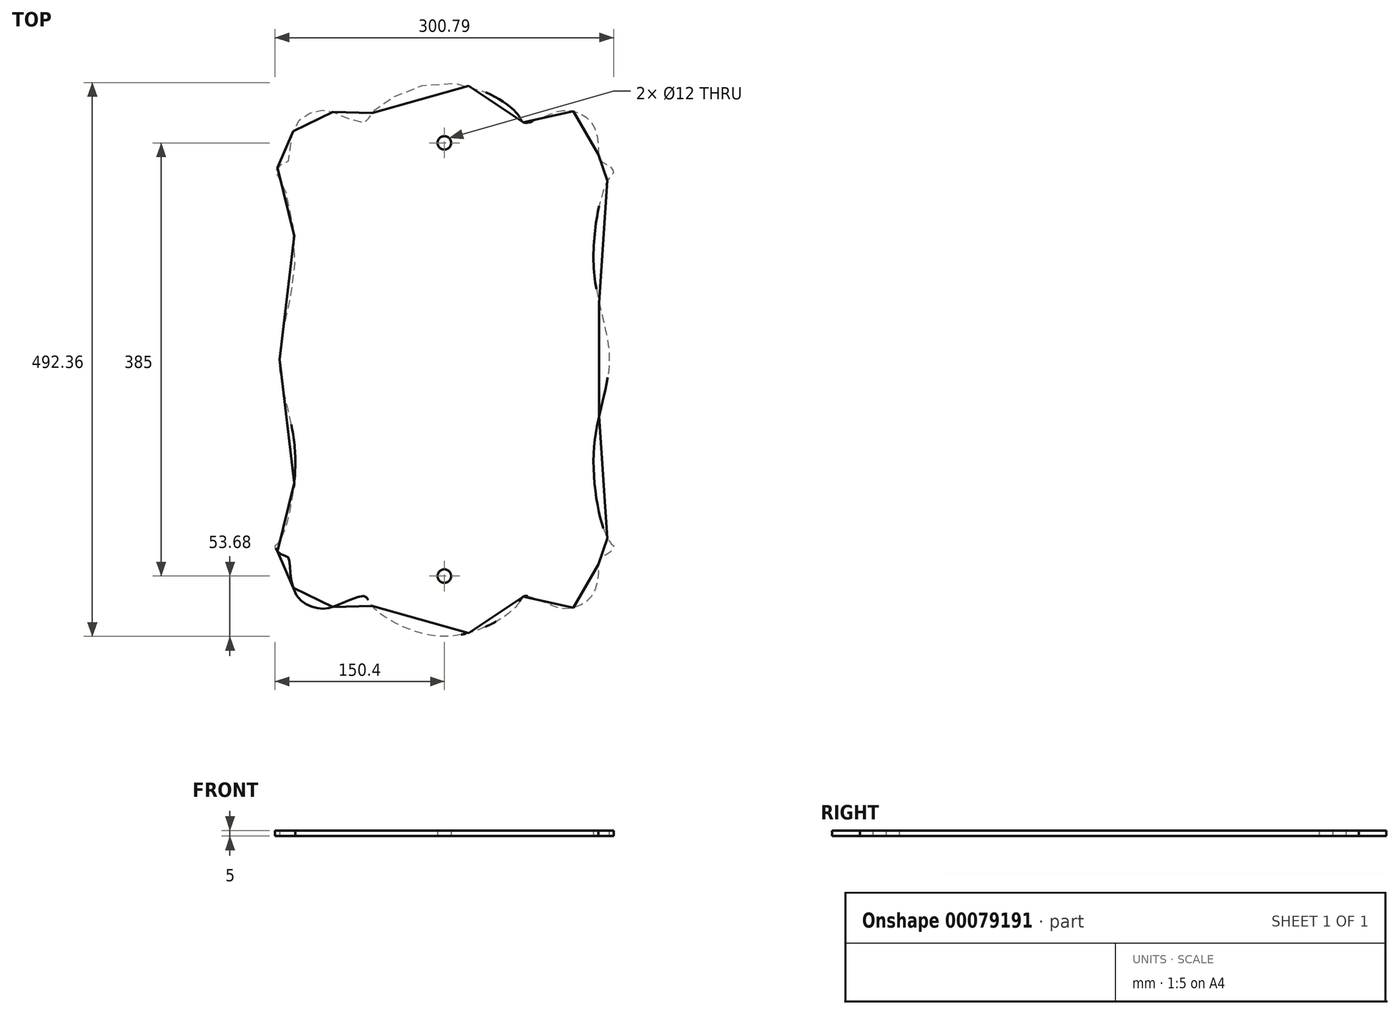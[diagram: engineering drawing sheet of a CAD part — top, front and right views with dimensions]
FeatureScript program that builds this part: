
annotation { "Feature Type Name" : "Feature", "Feature Type Description" : "" }
export const myFeature = defineFeature(function(context is Context, id is Id, definition is map)
    precondition{}
    {
        {
            var Q0;
            Q0=qCreatedBy(makeId("Top.planeOp"),FACE);
            var sketch = newSketch(context, id + "F0", { "sketchPlane" : qUnion([Q0])});
            skPoint(sketch, "E0", {"position": v(150.32, -165.76) * mm});
            skPoint(sketch, "E1", {"position": v(107.37, -221.56) * mm});
            skPoint(sketch, "E2", {"position": v(69.02, -211.72) * mm});
            skPoint(sketch, "E3", {"position": v(0, -246.18) * mm});
            skPoint(sketch, "E4", {"position": v(138.05, -177.25) * mm});
            skPoint(sketch, "E5", {"position": v(146.48, 0) * mm});
            skPoint(sketch, "E6", {"position": v(132.68, -82.88) * mm});
            skLineSegment(sketch, "E7", {"start": v(0, 292) * mm, "end": v(0, -246.18) * mm, "construction": true});
            skPoint(sketch, "E8.MirrorP", {"position": v(-146.48, 0) * mm});
            skPoint(sketch, "E9.MirrorP", {"position": v(-132.68, -82.88) * mm});
            skPoint(sketch, "E10.MirrorP", {"position": v(-150.32, -165.76) * mm});
            skPoint(sketch, "E11.MirrorP", {"position": v(-138.05, -177.25) * mm});
            skPoint(sketch, "E12.MirrorP", {"position": v(-107.37, -221.56) * mm});
            skPoint(sketch, "E13.MirrorP", {"position": v(-69.02, -211.72) * mm});
            skPoint(sketch, "E14", {"position": v(0, 0) * mm});
            skPoint(sketch, "E15", {"position": v(-146.25, -161.4) * mm});
            skPoint(sketch, "E16", {"position": v(-136.87, -189.28) * mm});
            skPoint(sketch, "E17", {"position": v(-146.26, -172.33) * mm});
            skPoint(sketch, "E18", {"position": v(-131.04, -210.06) * mm});
            skPoint(sketch, "E19", {"position": v(-94.82, -218.38) * mm});
            skPoint(sketch, "E20", {"position": v(-60.59, -222.84) * mm});
            skPoint(sketch, "E21", {"position": v(-67.25, -214.49) * mm});
            skPoint(sketch, "E22", {"position": v(-72.48, -210.2) * mm});
            skPoint(sketch, "E23", {"position": v(-119.37, -219.05) * mm});
            skPoint(sketch, "E24", {"position": v(-149.89, -167.68) * mm});
            skPoint(sketch, "E25.MirrorP", {"position": v(60.59, -222.84) * mm});
            skPoint(sketch, "E26.MirrorP", {"position": v(67.25, -214.49) * mm});
            skPoint(sketch, "E27.MirrorP", {"position": v(72.48, -210.2) * mm});
            skPoint(sketch, "E28.MirrorP", {"position": v(94.82, -218.38) * mm});
            skPoint(sketch, "E29.MirrorP", {"position": v(119.37, -219.05) * mm});
            skPoint(sketch, "E30.MirrorP", {"position": v(136.87, -189.28) * mm});
            skPoint(sketch, "E31.MirrorP", {"position": v(146.26, -172.33) * mm});
            skPoint(sketch, "E32.MirrorP", {"position": v(149.89, -167.68) * mm});
            skPoint(sketch, "E33.MirrorP", {"position": v(146.25, -161.4) * mm});
            skPoint(sketch, "E34", {"position": v(-139.73, -175.31) * mm});
            skPoint(sketch, "E35.MirrorP", {"position": v(131.04, -210.06) * mm});
            skPoint(sketch, "E36.MirrorP", {"position": v(-132.68, 82.88) * mm});
            skPoint(sketch, "E37.MirrorP", {"position": v(-139.73, 175.31) * mm});
            skPoint(sketch, "E38.MirrorP", {"position": v(-150.32, 165.76) * mm});
            skPoint(sketch, "E39.MirrorP", {"position": v(69.02, 211.72) * mm});
            skPoint(sketch, "E40.MirrorP", {"position": v(150.32, 165.76) * mm});
            skPoint(sketch, "E41.MirrorP", {"position": v(-67.25, 214.49) * mm});
            skPoint(sketch, "E42.MirrorP", {"position": v(131.04, 210.06) * mm});
            skPoint(sketch, "E43.MirrorP", {"position": v(60.59, 222.84) * mm});
            skPoint(sketch, "E44.MirrorP", {"position": v(119.37, 219.05) * mm});
            skPoint(sketch, "E45.MirrorP", {"position": v(136.87, 189.28) * mm});
            skPoint(sketch, "E46.MirrorP", {"position": v(-72.48, 210.2) * mm});
            skPoint(sketch, "E47.MirrorP", {"position": v(-138.05, 177.25) * mm});
            skPoint(sketch, "E48.MirrorP", {"position": v(-69.02, 211.72) * mm});
            skPoint(sketch, "E49.MirrorP", {"position": v(72.48, 210.2) * mm});
            skPoint(sketch, "E50.MirrorP", {"position": v(-146.25, 161.4) * mm});
            skPoint(sketch, "E51.MirrorP", {"position": v(-136.87, 189.28) * mm});
            skPoint(sketch, "E52.MirrorP", {"position": v(138.05, 177.25) * mm});
            skPoint(sketch, "E53.MirrorP", {"position": v(67.25, 214.49) * mm});
            skPoint(sketch, "E54.MirrorP", {"position": v(-149.89, 167.68) * mm});
            skPoint(sketch, "E55.MirrorP", {"position": v(149.89, 167.68) * mm});
            skPoint(sketch, "E56.MirrorP", {"position": v(-107.37, 221.56) * mm});
            skPoint(sketch, "E57.MirrorP", {"position": v(-94.82, 218.38) * mm});
            skPoint(sketch, "E58.MirrorP", {"position": v(146.26, 172.33) * mm});
            skPoint(sketch, "E59.MirrorP", {"position": v(107.37, 221.56) * mm});
            skPoint(sketch, "E60.MirrorP", {"position": v(-131.04, 210.06) * mm});
            skPoint(sketch, "E61.MirrorP", {"position": v(94.82, 218.38) * mm});
            skPoint(sketch, "E62.MirrorP", {"position": v(146.25, 161.4) * mm});
            skPoint(sketch, "E63.MirrorP", {"position": v(0, 246.18) * mm});
            skPoint(sketch, "E64.MirrorP", {"position": v(-146.26, 172.33) * mm});
            skPoint(sketch, "E65.MirrorP", {"position": v(-119.37, 219.05) * mm});
            skPoint(sketch, "E66.MirrorP", {"position": v(-60.59, 222.84) * mm});
            skPoint(sketch, "E67.MirrorP", {"position": v(132.68, 82.88) * mm});
            skFitSpline(sketch, "E68", {"points": [v(-146.48, 0) * mm, v(-132.68, 82.88) * mm, v(-146.25, 161.4) * mm, v(-150.32, 165.76) * mm, v(-149.89, 167.68) * mm, v(-146.26, 172.33) * mm, v(-139.73, 175.31) * mm, v(-138.05, 177.25) * mm, v(-136.87, 189.28) * mm, v(-131.04, 210.06) * mm, v(-119.37, 219.05) * mm, v(-107.37, 221.56) * mm, v(-94.82, 218.38) * mm, v(-72.48, 210.2) * mm, v(-69.02, 211.72) * mm, v(-67.25, 214.49) * mm, v(-60.59, 222.84) * mm, v(0, 246.18) * mm, v(60.59, 222.84) * mm, v(67.25, 214.49) * mm, v(69.02, 211.72) * mm, v(72.48, 210.2) * mm, v(94.82, 218.38) * mm, v(107.37, 221.56) * mm, v(119.37, 219.05) * mm, v(131.04, 210.06) * mm, v(136.87, 189.28) * mm, v(138.05, 177.25) * mm, v(146.26, 172.33) * mm, v(149.89, 167.68) * mm, v(150.32, 165.76) * mm, v(146.25, 161.4) * mm, v(132.68, 82.88) * mm, v(146.48, 0) * mm, v(132.68, -82.88) * mm, v(146.25, -161.4) * mm, v(150.32, -165.76) * mm, v(149.89, -167.68) * mm, v(146.26, -172.33) * mm, v(138.05, -177.25) * mm, v(136.87, -189.28) * mm, v(131.04, -210.06) * mm, v(119.37, -219.05) * mm, v(107.37, -221.56) * mm, v(94.82, -218.38) * mm, v(72.48, -210.2) * mm, v(69.02, -211.72) * mm, v(67.25, -214.49) * mm, v(60.59, -222.84) * mm, v(0, -246.18) * mm, v(-60.59, -222.84) * mm, v(-67.25, -214.49) * mm, v(-69.02, -211.72) * mm, v(-72.48, -210.2) * mm, v(-94.82, -218.38) * mm, v(-107.37, -221.56) * mm, v(-119.37, -219.05) * mm, v(-131.04, -210.06) * mm, v(-136.87, -189.28) * mm, v(-138.05, -177.25) * mm, v(-139.73, -175.31) * mm, v(-146.26, -172.33) * mm, v(-149.89, -167.68) * mm, v(-150.32, -165.76) * mm, v(-146.25, -161.4) * mm, v(-132.68, -82.88) * mm, v(-146.48, 0) * mm]});
            skPoint(sketch, "E69", {"position": v(0, 295) * mm});
            skPoint(sketch, "E70", {"position": v(-30, 295) * mm});
            skPoint(sketch, "E71", {"position": v(-225, 0) * mm});
            skPoint(sketch, "E72", {"position": v(-225, 100) * mm});
            skPoint(sketch, "E73.MirrorP", {"position": v(225, 100) * mm});
            skPoint(sketch, "E74.MirrorP", {"position": v(225, -60) * mm});
            skLineSegment(sketch, "E75", {"start": v(0, 0) * mm, "end": v(-373.3, 215.53) * mm, "construction": true});
            skLineSegment(sketch, "E76", {"start": v(0, 0) * mm, "end": v(-204.64, 354.44) * mm, "construction": true});
            skLineSegment(sketch, "E77", {"start": v(-225, 0) * mm, "end": v(-225, 100) * mm});
            skLineSegment(sketch, "E78", {"start": v(-30, 295) * mm, "end": v(0, 295) * mm});
            skPoint(sketch, "E79", {"position": v(-30, 100) * mm});
            skArc(sketch, "E80", {"start": v(-30, 295) * mm, "mid": v(-167.89, 237.89) * mm, "end": v(-225, 100) * mm});
            skLineSegment(sketch, "E81.MirrorCS", {"start": v(225, 0) * mm, "end": v(225, 100) * mm});
            skArc(sketch, "E82.MirrorCS", {"start": v(30, 295) * mm, "mid": v(167.89, 237.89) * mm, "end": v(225, 100) * mm});
            skLineSegment(sketch, "E83.MirrorCS", {"start": v(30, 295) * mm, "end": v(0, 295) * mm});
            skArc(sketch, "E84.MirrorCS", {"start": v(-30, -295) * mm, "mid": v(-167.89, -237.89) * mm, "end": v(-225, -100) * mm});
            skLineSegment(sketch, "E85.MirrorCS", {"start": v(-225, 0) * mm, "end": v(-225, -100) * mm});
            skLineSegment(sketch, "E86.MirrorCS", {"start": v(225, 0) * mm, "end": v(225, -100) * mm});
            skArc(sketch, "E87.MirrorCS", {"start": v(30, -295) * mm, "mid": v(167.89, -237.89) * mm, "end": v(225, -100) * mm});
            skLineSegment(sketch, "E88.MirrorCS", {"start": v(30, -295) * mm, "end": v(0, -295) * mm});
            skLineSegment(sketch, "E89.MirrorCS", {"start": v(-30, -295) * mm, "end": v(0, -295) * mm});
            skCircle(sketch, "E90", {"center": v(0, 192.5) * mm, "radius": 6 * mm});
            skCircle(sketch, "E91.MirrorC", {"center": v(0, -192.5) * mm, "radius": 6 * mm});
            skSolve(sketch);
        }
        {
            var Q0;
            Q0=makeQuery(id+"F0.imprint","IMPRINT",FACE,{"disambiguationData":[TD([[makeQuery(id+"F0.imprint","IMPRINT",EDGE,{"derivedFrom":sQuery(id+"F0.wireOp",EDGE,"E68")}),-1.0]])]});
            extrude(context, id + "F1", {"entities" : qUnion([Q0]), "depth" : 5 * mm, "symmetric" : true});
        }
        {
            var Q0;
            Q0=makeQuery(id+"F1.opExtrude","CAP_FACE",FACE,{"disambiguationData":[OSD([sQuery(id+"F0.wireOp",EDGE,"E68"),sQuery(id+"F0.wireOp",EDGE,"E90"),sQuery(id+"F0.wireOp",EDGE,"E91.MirrorC")])],"isStart":false});
            cPlane(context, id + "F2", {"entities" : qUnion([Q0]), "cplaneType" : CPlaneType.OFFSET, "offset" : 50 * mm, "width" : 150 * mm, "height" : 150 * mm});
        }
    });
